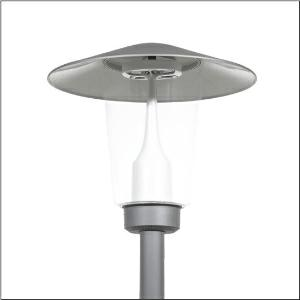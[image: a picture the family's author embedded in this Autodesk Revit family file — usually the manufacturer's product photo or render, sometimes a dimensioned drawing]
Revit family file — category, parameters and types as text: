
# Revit family: pilzleuchte_iq___st1_2a_5xa5235ef14h_b780
name_source: partatom
category: Lighting Fixtures
units: mm (PartAtom-declared; Revit-internal decimal feet)

## family parameters
Cut with Voids When Loaded = No
Host = Face
Light Source = No
Part Type = Normal
Room Calculation Point = No
Round Connector Dimension = Use Diameter
Shared = No

## types (1)
- --- (1 x LED, 1550 lm, 10.5 W, 3000K)
    Apparent Load = 11 VA
    CIE Flux Codes = 24 61 93 98 100
    Color Rendering = 70
    Color Temperature = 3000K
    Default Elevation = 1800 mm
    Description = Mushroom Luminaire iQ, mast luminaire, Module 540 iQ-SR, primary light control with 3 zone facetted reflector, of plastic, silver coated, highly specular, structured, primary optical cover: cover, of PMMA, transparent, light distribution: ST1.2a, light emission: direct distribution, primary light characteristic: asymmetric, installation type: post-top, LED, High Power LED, rated luminous flux: 1.550lm, luminous efficacy: 148lm/W, light colour: 730, colour temperature: 3000K, control gear: ECG iQ, control: Auto-Match, Temp-Guard, Lumen-Switch, Night-Set, Smart-Wire, Light-Fading, Desk-Remote (wireless, voltage-free reading and setting of iQ features in the workshop via application-optimized NFC function/RFID function), optimised constant luminous flux control (CLO 2.0), Street-Remote, presetting dimming logarithmic, with terminal, 6-pole, max. 2.5mm², mains connection: 230..240V, AC, 50/60Hz, start of lifetime: 11W, end of service life: 11W, reduction: 5W, luminaire housing, upper part, of glass-fibre reinforced polyester, coated, Siteco® metallic grey (DB 702S), diameter: 650mm, height: 586mm, spigot size: d x l = 76 x 70mm (post-top) | with reducer (optional accessory) 60 x 70mm, post-top mast mounting element, of diecast aluminium, coated, Siteco® metallic grey (DB 702S), Module 540 iQ-SR, traffic white (RAL 9016), equipment: standard, protection rating (complete): IP65, insulation class (complete): insulation class II (safety insulation), certification: CE, ENEC, VDE, packaging unit: 1 piece

Light Distribution: ST1.2a
    Height = 586 mm
    Lamp = 1 x LED
    Lamp Light Flux = 1550 lm
    Lamp Power = 10.5 W
    Lamp count = 1
    Length = 650 mm
    Luminous efficacy = 148 lm/W
    Manufacturer = Siteco
    ModVariant = No
    Model = 5XA5235EF14H
    Number of Poles = 1
    OnlyDefault = Yes
    Power Factor = 1
    Product Name = Pilzleuchte iQ | ST1.2a
    Product group = mast luminaire | pylon top
    ProductGroupID = 6100
    Protection Class = Protection class II
    Protection Degree = IP 65
    RLX_Detail_Level = 1
    RLX_Emergency_Light_Flux = 0 lm
    RLX_Emergency_Type = 0
    RLX_Emergency_Type_DB = No
    RlxData = <blob elided: 123305 chars, md5=b313c60d>
    Socket = socket
    Standby Power = 0 W
    System Light Flux = 1550 lm
    System Power = 11 W
    Type Comments = factory setting: luminous flux: 100 % | dim-lin: 254 | 419 mA
    Type Image = l_1006077.jpg
    URL = http://relux.com
    VarID = @adj_093089
    Voltage = 0 V
    Weight = 0.00 kg
    Width = 0 mm  [stored 0 ft]

note: [stored X ft] marks values corroborated as IEEE doubles in the binary element streams (Revit-internal decimal feet)

## geometry (parser evidence)
native form markers: Blend x4, Sweep x11
no freeform markers — native parametric forms only
